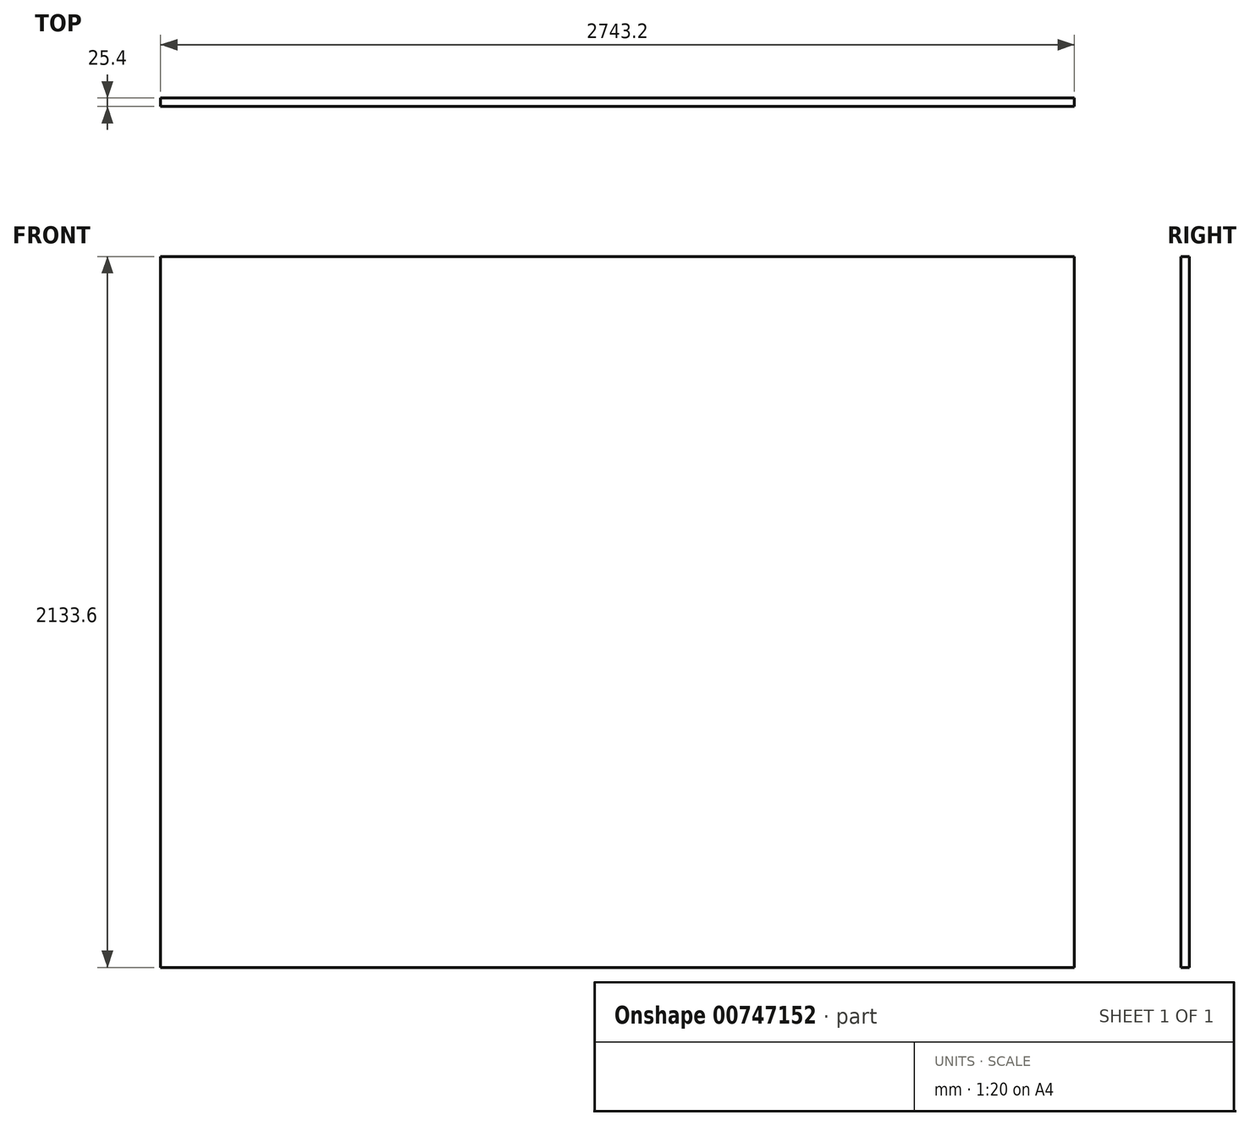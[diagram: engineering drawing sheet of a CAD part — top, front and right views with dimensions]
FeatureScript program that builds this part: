
annotation { "Feature Type Name" : "Feature", "Feature Type Description" : "" }
export const myFeature = defineFeature(function(context is Context, id is Id, definition is map)
    precondition{}
    {
        {
            var Q0;
            Q0=qCreatedBy(makeId("Right.planeOp"),FACE);
            var sketch = newSketch(context, id + "F0", { "sketchPlane" : qUnion([Q0])});
            skLineSegment(sketch, "E0.bottom", {"start": v(-57.6, 1811.27) * mm, "end": v(-32.2, 1811.27) * mm});
            skLineSegment(sketch, "E0.top", {"start": v(-57.6, -322.33) * mm, "end": v(-32.2, -322.33) * mm});
            skLineSegment(sketch, "E0.left", {"start": v(-57.6, 1811.27) * mm, "end": v(-57.6, -322.33) * mm});
            skLineSegment(sketch, "E0.right", {"start": v(-32.2, 1811.27) * mm, "end": v(-32.2, -322.33) * mm});
            skSolve(sketch);
        }
        {
            var Q0;
            Q0 = qSketchRegion(id + "F0", true);
            extrude(context, id + "F1", {"entities" : qUnion([Q0]), "oppositeDirection" : true, "depth" : 2743.2 * mm, "offsetDistance" : 25.4 * mm});
        }
    });
